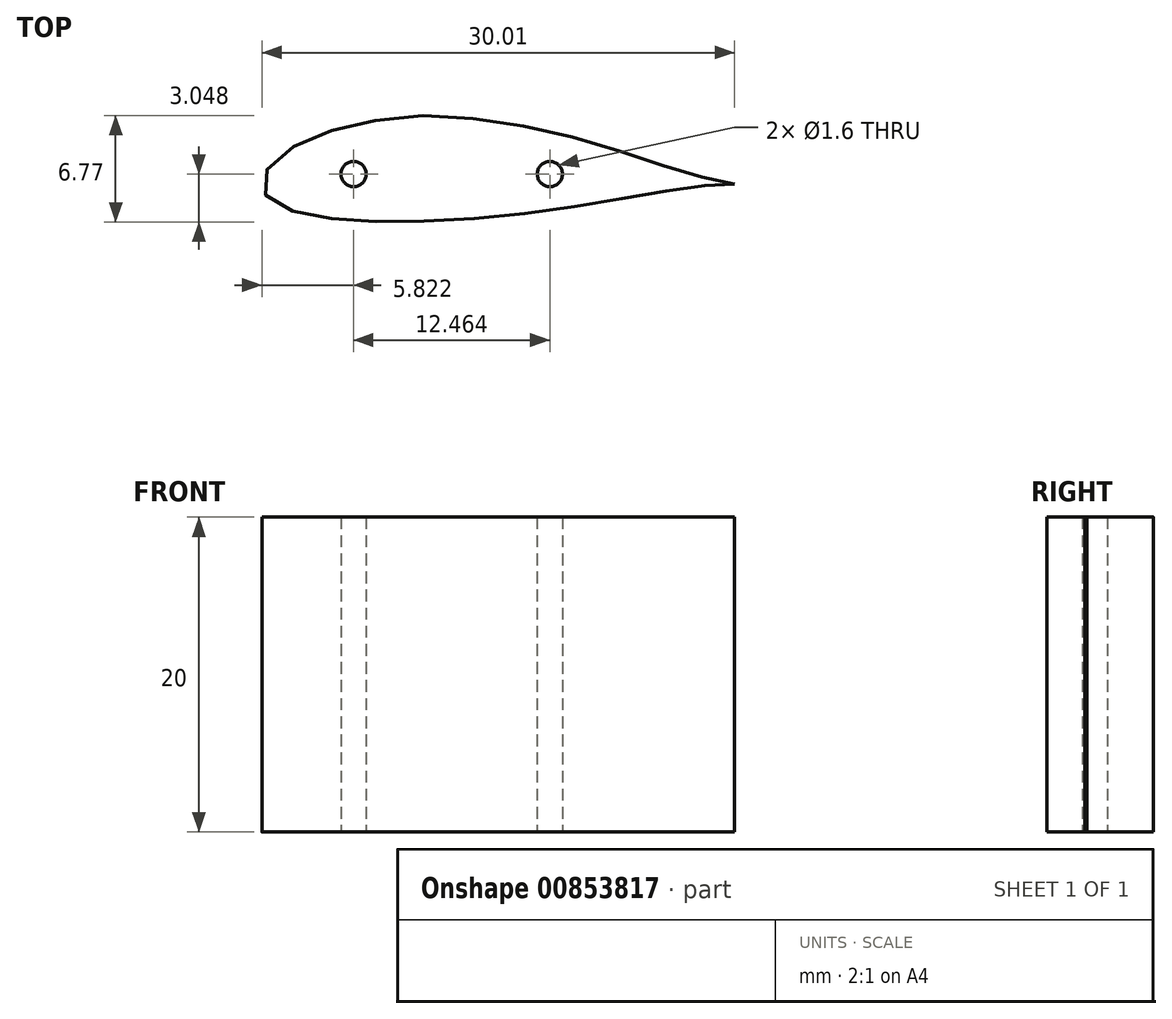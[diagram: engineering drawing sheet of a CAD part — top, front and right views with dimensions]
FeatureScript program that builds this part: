
annotation { "Feature Type Name" : "Feature", "Feature Type Description" : "" }
export const myFeature = defineFeature(function(context is Context, id is Id, definition is map)
    precondition{}
    {
        {
            var Q0;
            Q0=qCreatedBy(makeId("Top.planeOp"),FACE);
            var sketch = newSketch(context, id + "F0", { "sketchPlane" : qUnion([Q0])});
            skPoint(sketch, "E0", {"position": v(-46.96, 15.5) * mm});
            skPoint(sketch, "E1", {"position": v(-46.87, 16.06) * mm});
            skPoint(sketch, "E2", {"position": v(-46.97, 15.75) * mm});
            skPoint(sketch, "E3", {"position": v(-46.7, 16.34) * mm});
            skPoint(sketch, "E4", {"position": v(-46.49, 16.65) * mm});
            skPoint(sketch, "E5", {"position": v(-46.2, 16.94) * mm});
            skPoint(sketch, "E6", {"position": v(-45.85, 17.26) * mm});
            skPoint(sketch, "E7", {"position": v(-45.45, 17.56) * mm});
            skPoint(sketch, "E8", {"position": v(-44.99, 17.85) * mm});
            skPoint(sketch, "E9", {"position": v(-44.47, 18.13) * mm});
            skPoint(sketch, "E10", {"position": v(-43.89, 18.4) * mm});
            skPoint(sketch, "E11", {"position": v(-43.27, 18.66) * mm});
            skPoint(sketch, "E12", {"position": v(-42.58, 18.89) * mm});
            skPoint(sketch, "E13", {"position": v(-41.88, 19.1) * mm});
            skPoint(sketch, "E14", {"position": v(-41.13, 19.28) * mm});
            skPoint(sketch, "E15", {"position": v(-40.34, 19.43) * mm});
            skPoint(sketch, "E16", {"position": v(-39.51, 19.57) * mm});
            skPoint(sketch, "E17", {"position": v(-38.62, 19.67) * mm});
            skPoint(sketch, "E18", {"position": v(-37.73, 19.84) * mm});
            skPoint(sketch, "E19", {"position": v(-36.82, 19.84) * mm});
            skPoint(sketch, "E20", {"position": v(-35.87, 19.84) * mm});
            skPoint(sketch, "E21", {"position": v(-46.96, 15.23) * mm});
            skPoint(sketch, "E22", {"position": v(-46.86, 14.97) * mm});
            skPoint(sketch, "E23", {"position": v(-46.7, 14.74) * mm});
            skPoint(sketch, "E24", {"position": v(-46.5, 14.5) * mm});
            skPoint(sketch, "E25", {"position": v(-46.2, 14.28) * mm});
            skPoint(sketch, "E26", {"position": v(-45.85, 14.1) * mm});
            skPoint(sketch, "E27", {"position": v(-45.45, 13.9) * mm});
            skPoint(sketch, "E28", {"position": v(-44.97, 13.75) * mm});
            skPoint(sketch, "E29", {"position": v(-44.47, 13.62) * mm});
            skPoint(sketch, "E30", {"position": v(-43.88, 13.47) * mm});
            skPoint(sketch, "E31", {"position": v(-43.28, 13.36) * mm});
            skPoint(sketch, "E32", {"position": v(-42.59, 13.3) * mm});
            skPoint(sketch, "E33", {"position": v(-41.88, 13.23) * mm});
            skPoint(sketch, "E34", {"position": v(-41.13, 13.14) * mm});
            skPoint(sketch, "E35", {"position": v(-35.87, 13.16) * mm});
            skPoint(sketch, "E36", {"position": v(-34.92, 13.21) * mm});
            skPoint(sketch, "E37", {"position": v(-33, 19.6) * mm});
            skPoint(sketch, "E38", {"position": v(-32, 19.48) * mm});
            skPoint(sketch, "E39", {"position": v(-31.01, 19.28) * mm});
            skPoint(sketch, "E40", {"position": v(-33.95, 13.26) * mm});
            skPoint(sketch, "E41", {"position": v(-32.97, 13.33) * mm});
            skPoint(sketch, "E42", {"position": v(-32, 13.42) * mm});
            skPoint(sketch, "E43", {"position": v(-31.01, 13.54) * mm});
            skPoint(sketch, "E44", {"position": v(-30, 13.65) * mm});
            skPoint(sketch, "E45", {"position": v(-29.07, 13.79) * mm});
            skPoint(sketch, "E46", {"position": v(-28.12, 13.9) * mm});
            skPoint(sketch, "E47", {"position": v(-27.16, 14.06) * mm});
            skPoint(sketch, "E48", {"position": v(-26.25, 14.2) * mm});
            skPoint(sketch, "E49", {"position": v(-25.36, 14.38) * mm});
            skPoint(sketch, "E50", {"position": v(-24.5, 14.5) * mm});
            skPoint(sketch, "E51", {"position": v(-30, 19.12) * mm});
            skPoint(sketch, "E52", {"position": v(-29.07, 18.94) * mm});
            skPoint(sketch, "E53", {"position": v(-28.1, 18.7) * mm});
            skPoint(sketch, "E54", {"position": v(-27.18, 18.46) * mm});
            skPoint(sketch, "E55", {"position": v(-26.27, 18.18) * mm});
            skPoint(sketch, "E56", {"position": v(-25.36, 17.91) * mm});
            skPoint(sketch, "E57", {"position": v(-24.5, 17.68) * mm});
            skPoint(sketch, "E58", {"position": v(-23.65, 17.36) * mm});
            skPoint(sketch, "E59", {"position": v(-22.88, 17.14) * mm});
            skPoint(sketch, "E60", {"position": v(-23.67, 14.65) * mm});
            skPoint(sketch, "E61", {"position": v(-22.87, 14.8) * mm});
            skPoint(sketch, "E62", {"position": v(-22.1, 14.9) * mm});
            skPoint(sketch, "E63", {"position": v(-21.4, 15.04) * mm});
            skPoint(sketch, "E64", {"position": v(-20.75, 15.15) * mm});
            skPoint(sketch, "E65", {"position": v(-20.1, 15.25) * mm});
            skPoint(sketch, "E66", {"position": v(-19.54, 15.33) * mm});
            skPoint(sketch, "E67", {"position": v(-19.02, 15.39) * mm});
            skPoint(sketch, "E68", {"position": v(-16.96, 15.5) * mm});
            skPoint(sketch, "E69", {"position": v(-17.15, 15.5) * mm});
            skPoint(sketch, "E70", {"position": v(-17.3, 15.5) * mm});
            skPoint(sketch, "E71", {"position": v(-17.51, 15.5) * mm});
            skPoint(sketch, "E72", {"position": v(-17.82, 15.5) * mm});
            skPoint(sketch, "E73", {"position": v(-18.56, 15.43) * mm});
            skPoint(sketch, "E74", {"position": v(-18.17, 15.47) * mm});
            skPoint(sketch, "E75", {"position": v(-18.17, 15.7) * mm});
            skPoint(sketch, "E76", {"position": v(-17.83, 15.63) * mm});
            skPoint(sketch, "E77", {"position": v(-18.56, 15.8) * mm});
            skPoint(sketch, "E78", {"position": v(-17.54, 15.58) * mm});
            skPoint(sketch, "E79", {"position": v(-17.31, 15.53) * mm});
            skPoint(sketch, "E80", {"position": v(-17.15, 15.52) * mm});
            skPoint(sketch, "E81", {"position": v(-22.13, 16.88) * mm});
            skPoint(sketch, "E82", {"position": v(-21.4, 16.65) * mm});
            skPoint(sketch, "E83", {"position": v(-20.75, 16.43) * mm});
            skPoint(sketch, "E84", {"position": v(-20.13, 16.25) * mm});
            skPoint(sketch, "E85", {"position": v(-19.54, 16.08) * mm});
            skPoint(sketch, "E86", {"position": v(-19.02, 15.93) * mm});
            skPoint(sketch, "E87", {"position": v(-34.94, 19.75) * mm});
            skPoint(sketch, "E88", {"position": v(-33.96, 19.7) * mm});
            skPoint(sketch, "E89", {"position": v(-36.83, 13.13) * mm});
            skPoint(sketch, "E90", {"position": v(-40.35, 13.12) * mm});
            skPoint(sketch, "E91", {"position": v(-39.5, 13.1) * mm});
            skPoint(sketch, "E92", {"position": v(-38.64, 13.08) * mm});
            skPoint(sketch, "E93", {"position": v(-37.73, 13.09) * mm});
            skFitSpline(sketch, "E94", {"points": [v(-16.96, 15.5) * mm, v(-17.15, 15.52) * mm, v(-17.51, 15.5) * mm, v(-17.82, 15.5) * mm, v(-18.17, 15.47) * mm, v(-18.56, 15.43) * mm, v(-19.02, 15.39) * mm, v(-19.54, 15.33) * mm, v(-20.1, 15.25) * mm, v(-20.75, 15.15) * mm, v(-21.4, 15.04) * mm, v(-22.1, 14.9) * mm, v(-22.87, 14.8) * mm, v(-23.67, 14.65) * mm, v(-24.5, 14.5) * mm, v(-25.36, 14.38) * mm, v(-26.25, 14.2) * mm, v(-27.16, 14.06) * mm, v(-28.12, 13.9) * mm, v(-29.07, 13.79) * mm, v(-30, 13.65) * mm, v(-31.01, 13.54) * mm, v(-32, 13.42) * mm, v(-32.97, 13.33) * mm, v(-33.95, 13.26) * mm, v(-34.92, 13.21) * mm, v(-35.87, 13.16) * mm, v(-36.83, 13.13) * mm, v(-37.73, 13.09) * mm, v(-38.64, 13.08) * mm, v(-39.5, 13.1) * mm, v(-40.35, 13.12) * mm, v(-41.13, 13.14) * mm, v(-41.88, 13.23) * mm, v(-42.59, 13.3) * mm, v(-43.28, 13.36) * mm, v(-43.88, 13.47) * mm, v(-44.47, 13.62) * mm, v(-44.97, 13.75) * mm, v(-45.45, 13.9) * mm, v(-45.85, 14.1) * mm, v(-46.2, 14.28) * mm, v(-46.5, 14.5) * mm, v(-46.7, 14.74) * mm, v(-46.86, 14.97) * mm, v(-46.96, 15.23) * mm, v(-46.96, 15.5) * mm, v(-46.97, 15.75) * mm, v(-46.87, 16.06) * mm, v(-46.7, 16.34) * mm, v(-46.49, 16.65) * mm, v(-46.2, 16.94) * mm, v(-45.85, 17.26) * mm, v(-45.45, 17.56) * mm, v(-44.99, 17.85) * mm, v(-44.47, 18.13) * mm, v(-43.89, 18.4) * mm, v(-43.27, 18.66) * mm, v(-42.58, 18.89) * mm, v(-41.88, 19.1) * mm, v(-41.13, 19.28) * mm, v(-40.34, 19.43) * mm, v(-39.51, 19.57) * mm, v(-38.62, 19.67) * mm, v(-37.73, 19.84) * mm, v(-36.82, 19.84) * mm, v(-35.87, 19.84) * mm, v(-34.94, 19.75) * mm, v(-33.96, 19.7) * mm, v(-33, 19.6) * mm, v(-32, 19.48) * mm, v(-31.01, 19.28) * mm, v(-30, 19.12) * mm, v(-29.07, 18.94) * mm, v(-28.1, 18.7) * mm, v(-27.18, 18.46) * mm, v(-26.27, 18.18) * mm, v(-25.36, 17.91) * mm, v(-24.5, 17.68) * mm, v(-23.65, 17.36) * mm, v(-22.88, 17.14) * mm, v(-22.13, 16.88) * mm, v(-21.4, 16.65) * mm, v(-20.75, 16.43) * mm, v(-20.13, 16.25) * mm, v(-19.54, 16.08) * mm, v(-19.02, 15.93) * mm, v(-18.56, 15.8) * mm, v(-18.17, 15.7) * mm, v(-17.83, 15.63) * mm, v(-17.54, 15.63) * mm, v(-16.96, 15.5) * mm]});
            skCircle(sketch, "E95", {"center": v(-28.68, 16.13) * mm, "radius": 0.8 * mm});
            skCircle(sketch, "E96", {"center": v(-41.15, 16.13) * mm, "radius": 0.8 * mm});
            skSolve(sketch);
        }
        {
            var Q0;
            Q0=makeQuery(id+"F0.imprint","IMPRINT",FACE,{"disambiguationData":[TD([[makeQuery(id+"F0.imprint","IMPRINT",EDGE,{"derivedFrom":sQuery(id+"F0.wireOp",EDGE,"E94")}),-1.0]])]});
            extrude(context, id + "F1", {"entities" : qUnion([Q0]), "depth" : 20 * mm, "offsetDistance" : 25.4 * mm});
        }
    });
